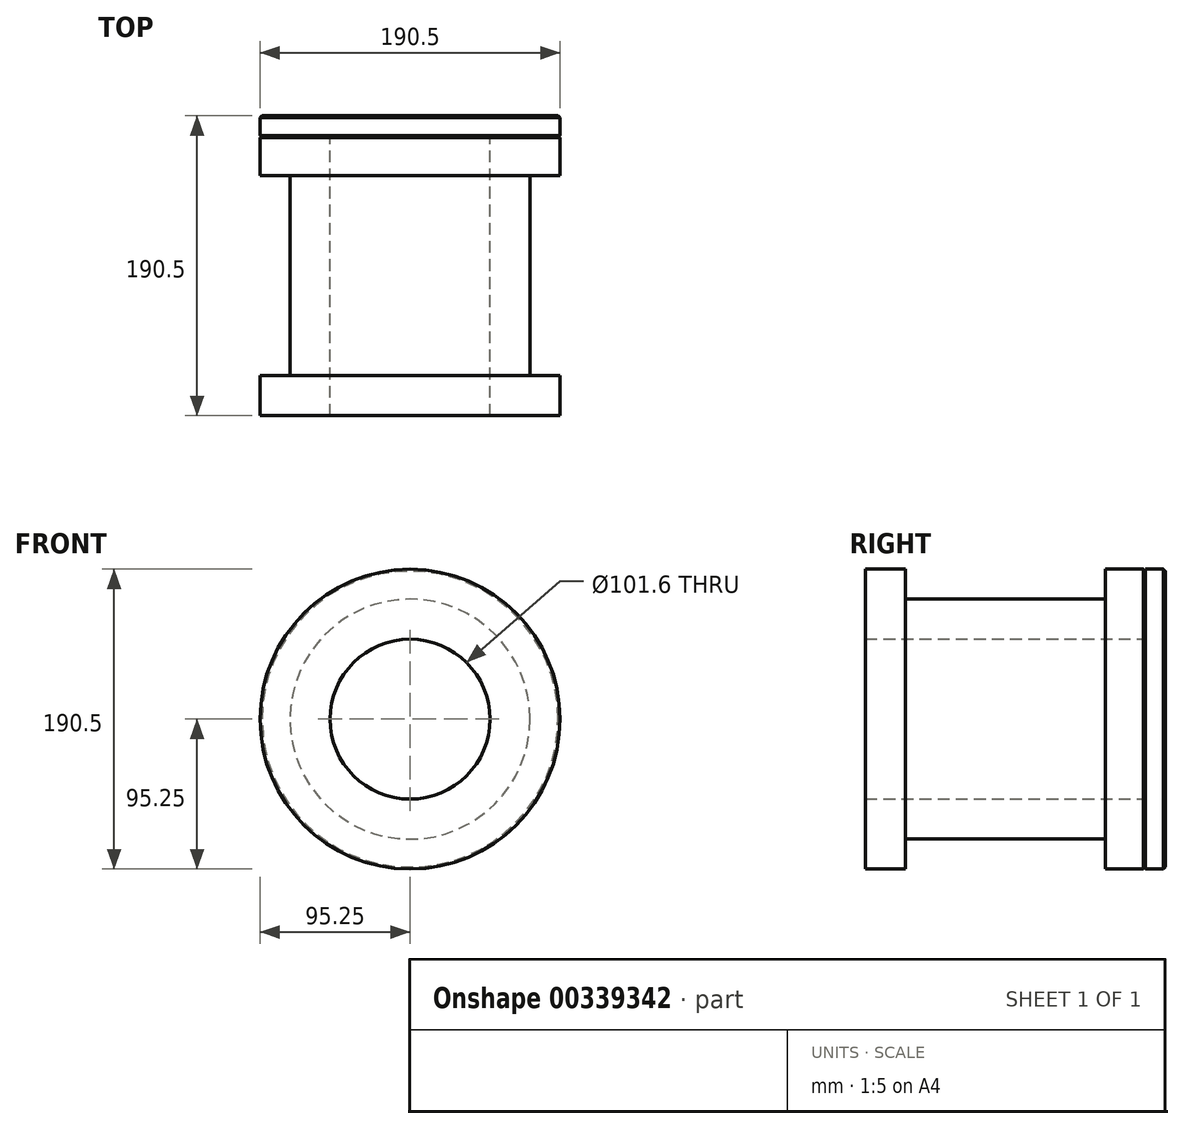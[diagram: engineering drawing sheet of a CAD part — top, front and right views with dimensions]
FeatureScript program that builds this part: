
annotation { "Feature Type Name" : "Feature", "Feature Type Description" : "" }
export const myFeature = defineFeature(function(context is Context, id is Id, definition is map)
    precondition{}
    {
        {
            var Q0;
            Q0=qCreatedBy(makeId("Right.planeOp"),FACE);
            var sketch = newSketch(context, id + "F0", { "sketchPlane" : qUnion([Q0])});
            skLineSegment(sketch, "E0", {"start": v(-52.84, 0) * mm, "end": v(74.16, 0) * mm});
            skSolve(sketch);
        }
        {
            var Q0;
            Q0=sQuery(id+"F0.wireOp",EDGE,"E0");
            var Q1;
            Q1=sQuery(id+"F0.wireOp",VERTEX,"E0.start");
            cPlane(context, id + "F1", {"entities" : qUnion([Q0, Q1]), "cplaneType" : CPlaneType.LINE_POINT, "offset" : 25.4 * mm, "width" : 152.4 * mm, "height" : 152.4 * mm});
        }
        {
            var Q0;
            Q0=qCreatedBy(id+"F1.planeOp",FACE);
            var sketch = newSketch(context, id + "F2", { "sketchPlane" : qUnion([Q0])});
            skCircle(sketch, "E1", {"center": v(0, 0) * mm, "radius": 76.2 * mm});
            skCircle(sketch, "E2", {"center": v(0, 0) * mm, "radius": 95.25 * mm});
            skSolve(sketch);
        }
        {
            var Q0;
            Q0=makeQuery(id+"F2.imprint","IMPRINT",FACE,{"disambiguationData":[TD([[makeQuery(id+"F2.imprint","IMPRINT",EDGE,{"derivedFrom":sQuery(id+"F2.wireOp",EDGE,"E1")}),-1.0]])]});
            var Q1;
            Q1=sQuery(id+"F0.wireOp",EDGE,"E0");
            sweep(context, id + "F3", {"profiles" : qUnion([Q0]), "path" : qUnion([Q1])});
        }
        {
            var Q0;
            Q0=makeQuery(id+"F3.opSweep","SWEPT_FACE",FACE,{"disambiguationData":[OSD([sQuery(id+"F0.wireOp",EDGE,"E0"),sQuery(id+"F2.wireOp",EDGE,"E2")])]});
            shell(context, id + "F4", {"entities" : qUnion([Q0]), "thickness" : 25.4 * mm, "oppositeDirection" : true});
        }
        {
            var Q0;
            Q0=makeQuery(id+"F3.opSweep","CAP_FACE",FACE,{"disambiguationData":[OSD([sQuery(id+"F0.wireOp",VERTEX,"E0.end"),sQuery(id+"F2.wireOp",EDGE,"E1"),sQuery(id+"F2.wireOp",EDGE,"E2")])],"isStart":false});
            cPlane(context, id + "F5", {"entities" : qUnion([Q0]), "cplaneType" : CPlaneType.OFFSET, "offset" : 0 * mm, "width" : 152.4 * mm, "height" : 152.4 * mm});
        }
        {
            var Q0;
            Q0=qCreatedBy(id+"F5.planeOp",FACE);
            var sketch = newSketch(context, id + "F6", { "sketchPlane" : qUnion([Q0])});
            skCircle(sketch, "E3", {"center": v(0, 0) * mm, "radius": 95.25 * mm});
            skSolve(sketch);
        }
        {
            var Q0;
            Q0=makeQuery(id+"F6.imprint","IMPRINT",FACE,{"disambiguationData":[TD([[makeQuery(id+"F6.imprint","IMPRINT",EDGE,{"derivedFrom":sQuery(id+"F6.wireOp",EDGE,"E3")}),1.0]])]});
            extrude(context, id + "F7", {"entities" : qUnion([Q0]), "depth" : 12.7 * mm, "offsetDistance" : 25.4 * mm});
        }
        {
            var Q0;
            Q0=makeQuery(id+"F3.opSweep","CAP_EDGE",EDGE,{"disambiguationData":[OSD([sQuery(id+"F0.wireOp",VERTEX,"E0.end"),sQuery(id+"F2.wireOp",EDGE,"E2")])],"isStart":false});
            var Q1;
            Q1=makeQuery(id+"F7.opExtrude","CAP_EDGE",EDGE,{"disambiguationData":[OSD([sQuery(id+"F6.wireOp",EDGE,"E3")])],"isStart":false});
            chamfer(context, id + "F8", {"entities" : qUnion([Q0, Q1]), "width" : 1.27 * mm, "tangentPropagation" : true});
        }
    });
